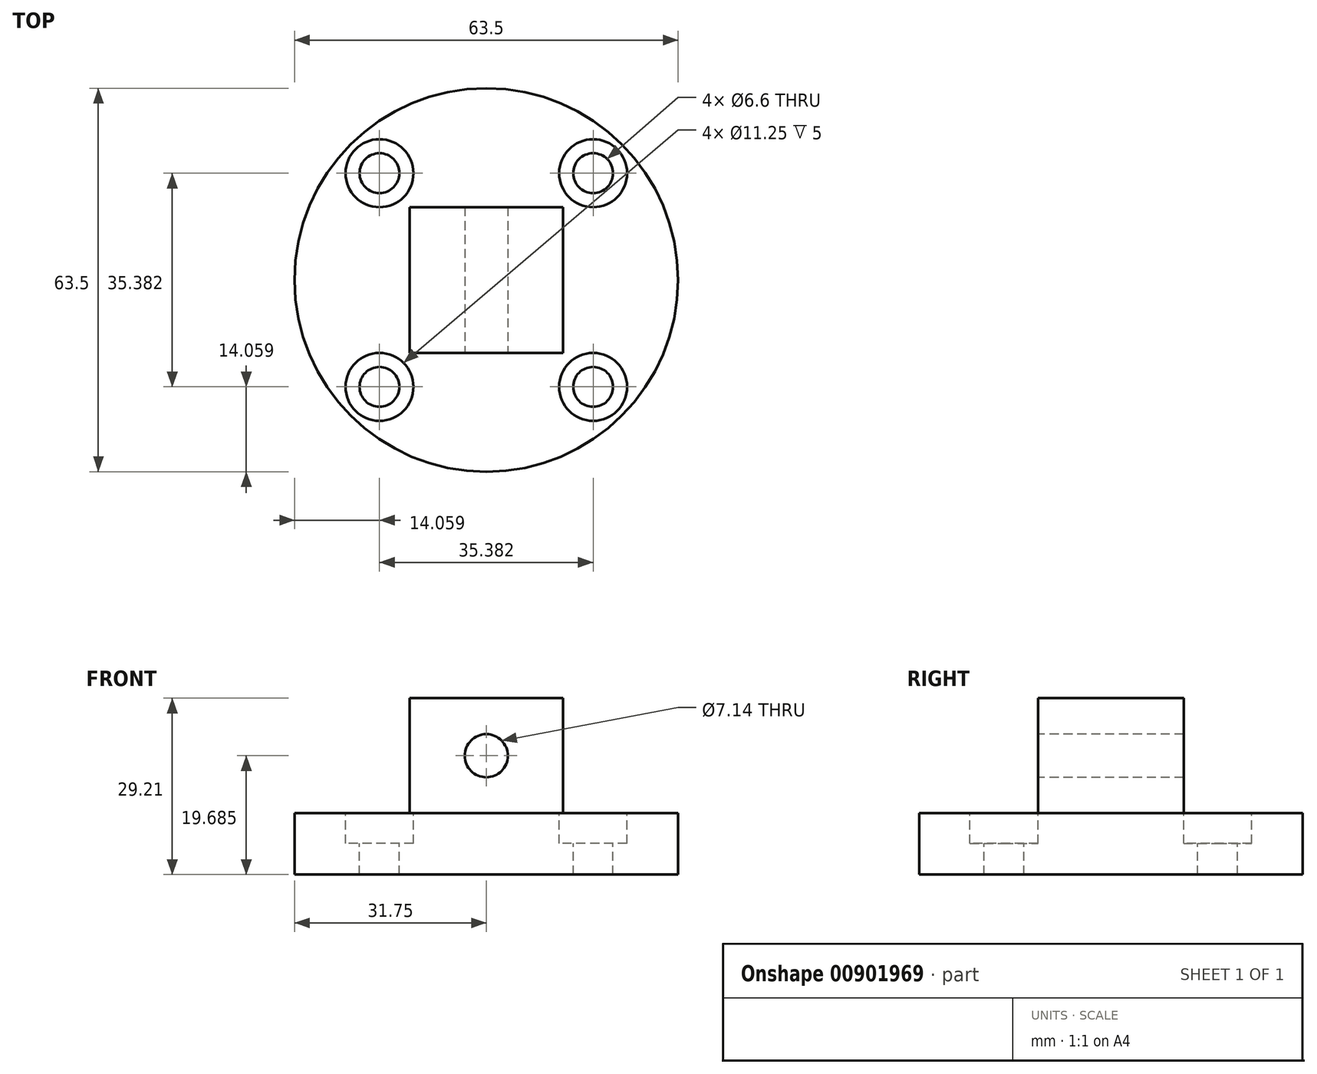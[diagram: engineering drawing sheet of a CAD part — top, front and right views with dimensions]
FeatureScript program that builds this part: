
annotation { "Feature Type Name" : "Feature", "Feature Type Description" : "" }
export const myFeature = defineFeature(function(context is Context, id is Id, definition is map)
    precondition{}
    {
        {
            var Q0;
            Q0=qCreatedBy(makeId("Top.planeOp"),FACE);
            var sketch = newSketch(context, id + "F0", { "sketchPlane" : qUnion([Q0])});
            skCircle(sketch, "E0", {"center": v(0, 0) * mm, "radius": 31.75 * mm});
            skSolve(sketch);
        }
        {
            var Q0;
            Q0 = qSketchRegion(id + "F0", true);
            extrude(context, id + "F1", {"entities" : qUnion([Q0]), "depth" : 10.16 * mm, "offsetDistance" : 25.4 * mm});
        }
        {
            var Q0;
            Q0=makeQuery(id+"F1.opExtrude","CAP_FACE",FACE,{"disambiguationData":[OSD([sQuery(id+"F0.wireOp",EDGE,"E0")])],"isStart":false});
            var sketch = newSketch(context, id + "F2", { "sketchPlane" : qUnion([Q0])});
            skLineSegment(sketch, "E1.bottom", {"start": v(12.7, 12.07) * mm, "end": v(-12.7, 12.07) * mm});
            skLineSegment(sketch, "E1.top", {"start": v(12.7, -12.07) * mm, "end": v(-12.7, -12.07) * mm});
            skLineSegment(sketch, "E1.left", {"start": v(12.7, 12.07) * mm, "end": v(12.7, -12.07) * mm});
            skLineSegment(sketch, "E1.right", {"start": v(-12.7, 12.07) * mm, "end": v(-12.7, -12.07) * mm});
            skPoint(sketch, "E1.middle", {"position": v(0, 0) * mm});
            skSolve(sketch);
        }
        {
            var Q0;
            Q0 = qSketchRegion(id + "F2", true);
            extrude(context, id + "F3", {"entities" : qUnion([Q0]), "operationType" : NewBodyOperationType.ADD, "depth" : 19.05 * mm, "offsetDistance" : 25.4 * mm});
        }
        {
            var Q0;
            Q0=makeQuery(id+"F1.opExtrude","CAP_FACE",FACE,{"disambiguationData":[OSD([sQuery(id+"F0.wireOp",EDGE,"E0")])],"isStart":false});
            var sketch = newSketch(context, id + "F4", { "sketchPlane" : qUnion([Q0])});
            skPoint(sketch, "E2.startSnap0", {"position": v(-12.7, 0) * mm});
            skCircle(sketch, "E3", {"center": v(0, 0) * mm, "radius": 25.02 * mm});
            skPoint(sketch, "E4", {"position": v(17.7, 17.7) * mm});
            skPoint(sketch, "E5", {"position": v(-17.7, 17.7) * mm});
            skPoint(sketch, "E6", {"position": v(-17.7, -17.7) * mm});
            skPoint(sketch, "E7", {"position": v(17.7, -17.7) * mm});
            skLineSegment(sketch, "E8", {"start": v(-25.02, 0) * mm, "end": v(25.02, 0) * mm});
            skLineSegment(sketch, "E9", {"start": v(-17.7, -17.7) * mm, "end": v(17.7, 17.7) * mm});
            skSolve(sketch);
        }
        {
            var Q0;
            Q0=sQuery(id+"F4.wireOp",VERTEX,"E5");
            var Q1;
            Q1=sQuery(id+"F4.wireOp",VERTEX,"E4");
            var Q2;
            Q2=sQuery(id+"F4.wireOp",VERTEX,"E6");
            var Q3;
            Q3=sQuery(id+"F4.wireOp",VERTEX,"E7");
            var Q4;
            Q4=makeQuery(id+"F1.opExtrude","SWEPT_BODY",BODY,{"disambiguationData":[OSD([sQuery(id+"F0.wireOp",EDGE,"E0")])]});
            hole(context, id + "F5", {"style" : HoleStyle.C_BORE, "endStyle" : HoleEndStyle.THROUGH, "holeDiameter" : 6.6 * mm, "cBoreDiameter" : 11.25 * mm, "cBoreDepth" : 5 * mm, "majorDiameter" : 6.35 * mm, "isTappedThrough" : true, "tappedDepth" : 12.7 * mm, "tapClearance" : 3, "startFromSketch" : true, "locations" : qUnion([Q0, Q1, Q2, Q3]), "scope" : qUnion([Q4])});
        }
        {
            var Q0;
            Q0=makeQuery(id+"F3.opExtrude","SWEPT_FACE",FACE,{"disambiguationData":[OSD([sQuery(id+"F2.wireOp",EDGE,"E1.top")])]});
            var sketch = newSketch(context, id + "F6", { "sketchPlane" : qUnion([Q0])});
            skPoint(sketch, "E10", {"position": v(0, 19.69) * mm});
            skSolve(sketch);
        }
        {
            var Q0;
            Q0=sQuery(id+"F6.wireOp",VERTEX,"E10");
            var Q1;
            Q1=makeQuery(id+"F1.opExtrude","SWEPT_BODY",BODY,{"disambiguationData":[OSD([sQuery(id+"F0.wireOp",EDGE,"E0")])]});
            hole(context, id + "F7", {"style" : HoleStyle.SIMPLE, "endStyle" : HoleEndStyle.THROUGH, "standardTappedOrClearance" : lookupTablePath({ "fit" : "Normal (ASME)", "standard" : "ANSI", "size" : "1/4", "type" : "Clearance" }), "standardBlindInLast" : lookupTablePath({ "fit" : "Normal", "standard" : "ANSI", "size" : "1/4", "type" : "Clearance" }), "holeDiameter" : 7.14 * mm, "majorDiameter" : 6.35 * mm, "isTappedThrough" : true, "tappedDepth" : 12.7 * mm, "tapClearance" : 3, "startFromSketch" : true, "locations" : qUnion([Q0]), "scope" : qUnion([Q1])});
        }
    });
